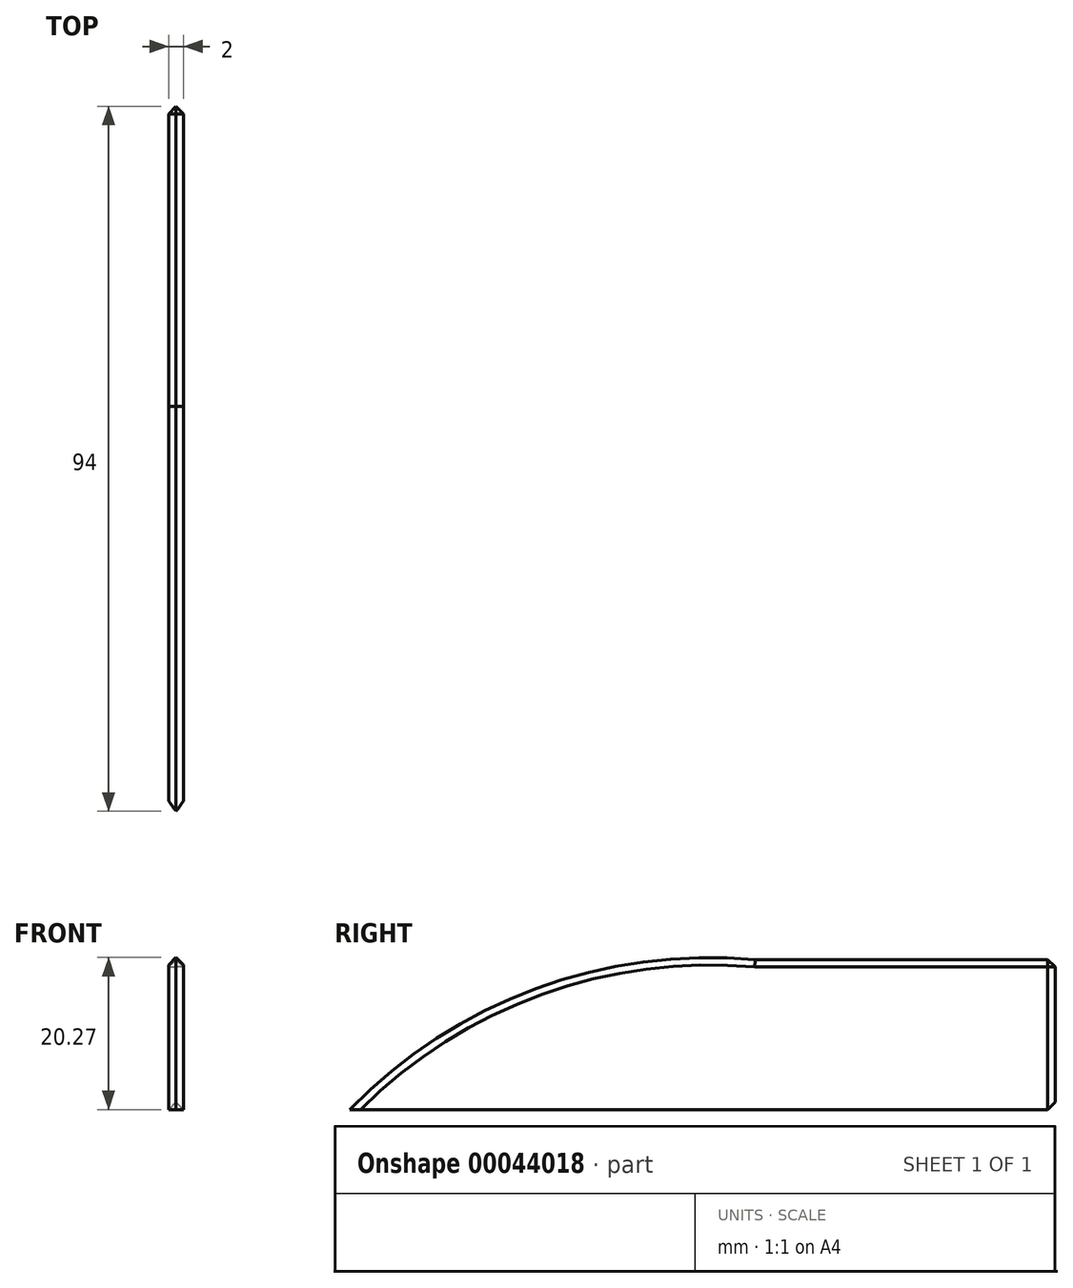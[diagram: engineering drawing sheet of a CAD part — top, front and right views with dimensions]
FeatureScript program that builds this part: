
annotation { "Feature Type Name" : "Feature", "Feature Type Description" : "" }
export const myFeature = defineFeature(function(context is Context, id is Id, definition is map)
    precondition{}
    {
        {
            var Q0;
            Q0=qCreatedBy(makeId("Top.planeOp"),FACE);
            var sketch = newSketch(context, id + "F0", { "sketchPlane" : qUnion([Q0])});
            skLineSegment(sketch, "E0.rect.bottom", {"start": v(0.95, 47) * mm, "end": v(-0.95, 47) * mm});
            skLineSegment(sketch, "E0.rect.top", {"start": v(0.95, -47) * mm, "end": v(-0.95, -47) * mm});
            skLineSegment(sketch, "E0.rect.left", {"start": v(0.95, 47) * mm, "end": v(0.95, -47) * mm});
            skLineSegment(sketch, "E0.rect.right", {"start": v(-0.95, 47) * mm, "end": v(-0.95, -47) * mm});
            skPoint(sketch, "E0.rect.middle", {"position": v(0, 0) * mm});
            skSolve(sketch);
        }
        {
            var Q0;
            Q0=qCreatedBy(makeId("Right.planeOp"),FACE);
            var sketch = newSketch(context, id + "F1", { "sketchPlane" : qUnion([Q0])});
            skLineSegment(sketch, "E1.bottom", {"start": v(47, 0) * mm, "end": v(-47, 0) * mm, "construction": true});
            skLineSegment(sketch, "E1.top", {"start": v(47, 20) * mm, "end": v(-47, 20) * mm, "construction": true});
            skLineSegment(sketch, "E1.left", {"start": v(47, 0) * mm, "end": v(47, 20) * mm, "construction": true});
            skLineSegment(sketch, "E1.right", {"start": v(-47, 0) * mm, "end": v(-47, 20) * mm, "construction": true});
            skArc(sketch, "E2", {"start": v(7, 20) * mm, "mid": v(-22.26, 16.1) * mm, "end": v(-47, 0) * mm});
            skLineSegment(sketch, "E3", {"start": v(7, 20) * mm, "end": v(47, 20) * mm});
            skLineSegment(sketch, "E4", {"start": v(47, 0) * mm, "end": v(47, 20) * mm});
            skLineSegment(sketch, "E5", {"start": v(47, 0) * mm, "end": v(-47, 0) * mm});
            skSolve(sketch);
        }
        {
            var Q0;
            Q0=makeQuery(id+"F1.imprint","IMPRINT",FACE,{"disambiguationData":[TD([[makeQuery(id+"F1.imprint","IMPRINT",EDGE,{"derivedFrom":sQuery(id+"F1.wireOp",EDGE,"E2")}),1.0]])]});
            extrude(context, id + "F2", {"entities" : qUnion([Q0]), "depth" : 1 * mm, "hasSecondDirection" : true, "secondDirectionOppositeDirection" : true, "secondDirectionDepth" : 1 * mm});
        }
        {
            var Q0;
            Q0=makeQuery(id+"F2.opExtrude","CAP_EDGE",EDGE,{"disambiguationData":[OSD([sQuery(id+"F1.wireOp",EDGE,"E2")])],"isStart":false});
            var Q1;
            Q1=makeQuery(id+"F2.opExtrude","CAP_EDGE",EDGE,{"disambiguationData":[OSD([sQuery(id+"F1.wireOp",EDGE,"E2")])],"isStart":true});
            var Q2;
            Q2=makeQuery(id+"F2.opExtrude","CAP_EDGE",EDGE,{"disambiguationData":[OSD([sQuery(id+"F1.wireOp",EDGE,"E3")])],"isStart":false});
            var Q3;
            Q3=makeQuery(id+"F2.opExtrude","CAP_EDGE",EDGE,{"disambiguationData":[OSD([sQuery(id+"F1.wireOp",EDGE,"E3")])],"isStart":true});
            var Q4;
            Q4=makeQuery(id+"F2.opExtrude","CAP_EDGE",EDGE,{"disambiguationData":[OSD([sQuery(id+"F1.wireOp",EDGE,"E4")])],"isStart":false});
            var Q5;
            Q5=makeQuery(id+"F2.opExtrude","SWEPT_FACE",FACE,{"disambiguationData":[OSD([sQuery(id+"F1.wireOp",EDGE,"E4")])]});
            chamfer(context, id + "F3", {"entities" : qUnion([Q0, Q1, Q2, Q3, Q4, Q5]), "width" : 1 * mm, "tangentPropagation" : true});
        }
    });
